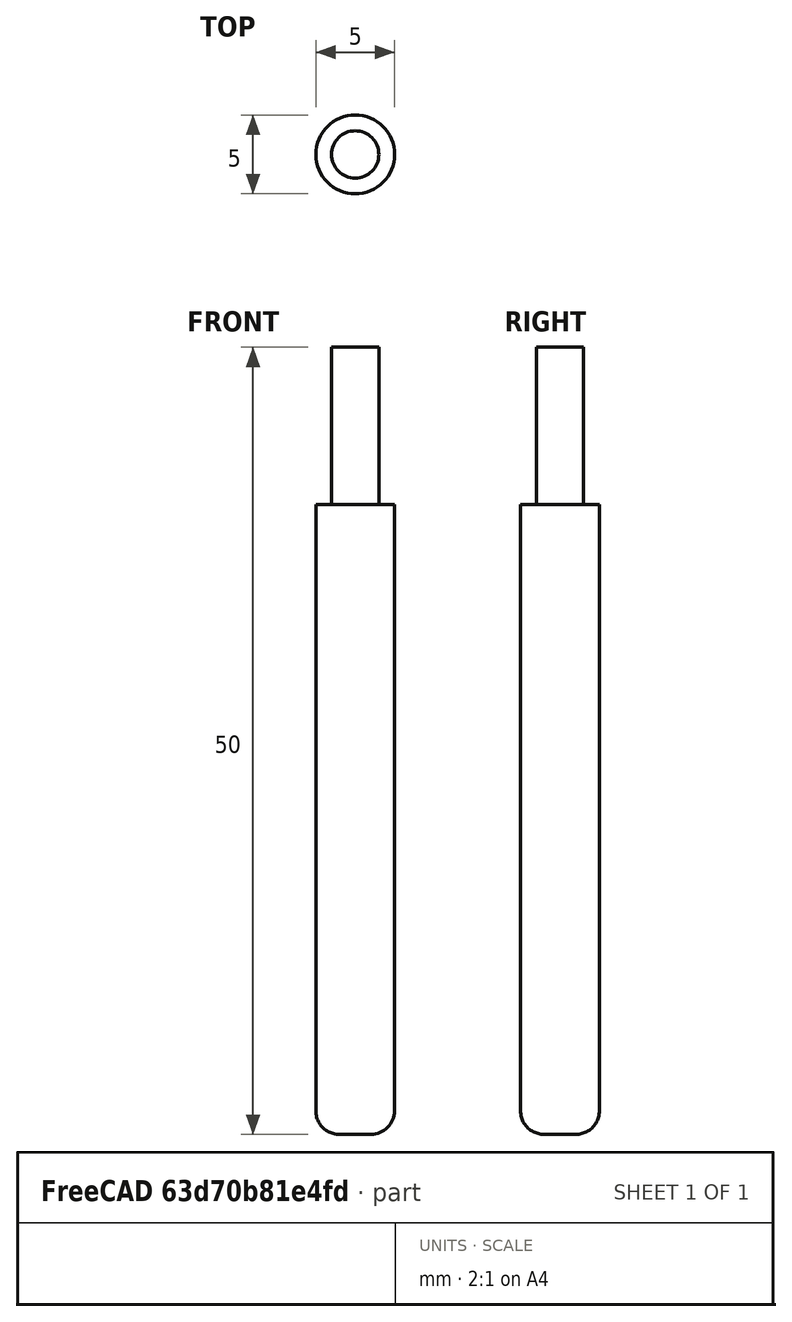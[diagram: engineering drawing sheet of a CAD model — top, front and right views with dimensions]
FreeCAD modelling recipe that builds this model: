
FCSTD DOCUMENT  (FreeCAD 1.1R43425 +8 (Git))
Label: bullnose
License: Creative Commons Attribution 4.0
LicenseURL: https://creativecommons.org/licenses/by/4.0/
objects: Sketcher::SketchObject×1, PartDesign::Revolution×1, App::FeaturePython×1, PartDesign::Body×1, App::Point×1
note: 6 computed .brp shape members not serialized (recipe doc carries the construction recipe); baked Part::Feature solids carry a one-line shape summary decoded from their .brp

FEATURE [Sketcher::SketchObject] Sketch
  ArcFitTolerance = 0
  AttachmentSupport = -> [XZ_Plane]
  ExternalTypes = [0]
  FullyConstrained = true
  MakeInternals = false
  MapMode = 5
  Placement = pos=(0,0,0) rot=(1,0,0;1.5708rad)
  expr: Constraints[12] = <<Attributes>>.ShankDiameter
  expr: Constraints[19] = <<Attributes>>.CuttingEdgeHeight
  expr: Constraints[23] = <<Attributes>>.CornerRadius
  expr: Constraints[5] = <<Attributes>>.Diameter
  expr: Constraints[6] = <<Attributes>>.Length
  sketch-geometry (9):
    g0: LineSegment StartX=0 StartY=50 StartZ=0 EndX=0 EndY=1.279e-13 EndZ=0
    g1: LineSegment StartX=0 StartY=1.279e-13 StartZ=0 EndX=1 EndY=1.279e-13 EndZ=0
    g2: LineSegment StartX=2.5 StartY=1.5 StartZ=0 EndX=2.5 EndY=40 EndZ=0
    g3: LineSegment StartX=1.5 StartY=50 StartZ=0 EndX=0 EndY=50 EndZ=0
    g4: LineSegment [constr] StartX=2.5 StartY=0 StartZ=0 EndX=-2.5 EndY=0 EndZ=0
    g5: LineSegment StartX=1.5 StartY=40.01 StartZ=0 EndX=2.5 EndY=40 EndZ=0
    g6: LineSegment StartX=1.5 StartY=50 StartZ=0 EndX=1.5 EndY=40.01 EndZ=0
    g7: LineSegment [constr] StartX=-1.5 StartY=50 StartZ=0 EndX=1.5 EndY=50 EndZ=0
    g8: ArcOfCircle CenterX=1 CenterY=1.5 CenterZ=0 NormalX=0 NormalY=0 NormalZ=1 AngleXU=0 Radius=1.5 StartAngle=4.71239 EndAngle=6.28319
  constraints (24):
    c: Vertical(g0)
    c: Coincident(g0,g1)
    c: Horizontal(g1)
    c: Vertical(g2)
    c: Horizontal(g3)
    c: DistanceX(g4,g4) = 5
    c: DistanceY(g4,g3) = 50
    c: Coincident(g2,g5)
    c: Vertical(g6)
    c: Coincident(g3,g6)
    c: Symmetric(g7,g7,g0)
    c: Coincident(g7,g3)
    c: DistanceX(g7,g7) = 3
    c: Coincident(g5,g6)
    c: Tangent(g1,g8) = -1.5708
    c: Tangent(g2,g8) = -1.5708
    c: PointOnObject(g0,g4)
    c: Symmetric(g4,g4,g-2)
    c: Vertical(g4,g2)
    c: DistanceY(g1,g2) = 40
    c: Coincident(g0,g3)
    c: Coincident(g-1,g0)
    c: DistanceY(g2,g5) = 0.01
    c: Radius(g8) = 1.5
FEATURE [PartDesign::Revolution] Revolution
  AllowMultiFace = false
  Angle = 360
  Angle2 = 60
  Axis = (0,2e-16,1)
  Base = (0,0,0)
  Placement = pos=(0,0,0) rot=(1,0,0;1.5708rad)
  Profile = -> Sketch
  ReferenceAxis = -> Sketch [V_Axis]
  Reversed = true
  Suppressed = false
  Type = 0
FEATURE [App::FeaturePython] PropertyBag  label="Attributes"  # WARN: FeaturePython — macro-defined, semantics opaque (R4)
  CornerRadius = 1.5
  CustomPropertyGroups = 1
  CuttingEdgeHeight = 40
  Diameter = 5
  Flutes = 4
  Length = 50
  ShankDiameter = 3
FEATURE [PartDesign::Body] Body  label="Bullnose"
  AllowCompound = false
  Group = -> [Sketch,Revolution,PropertyBag]
  Origin = -> Origin
  Tip = -> Revolution
FEATURE [App::Point] Origin001  label="Origin"
  Role = Origin
